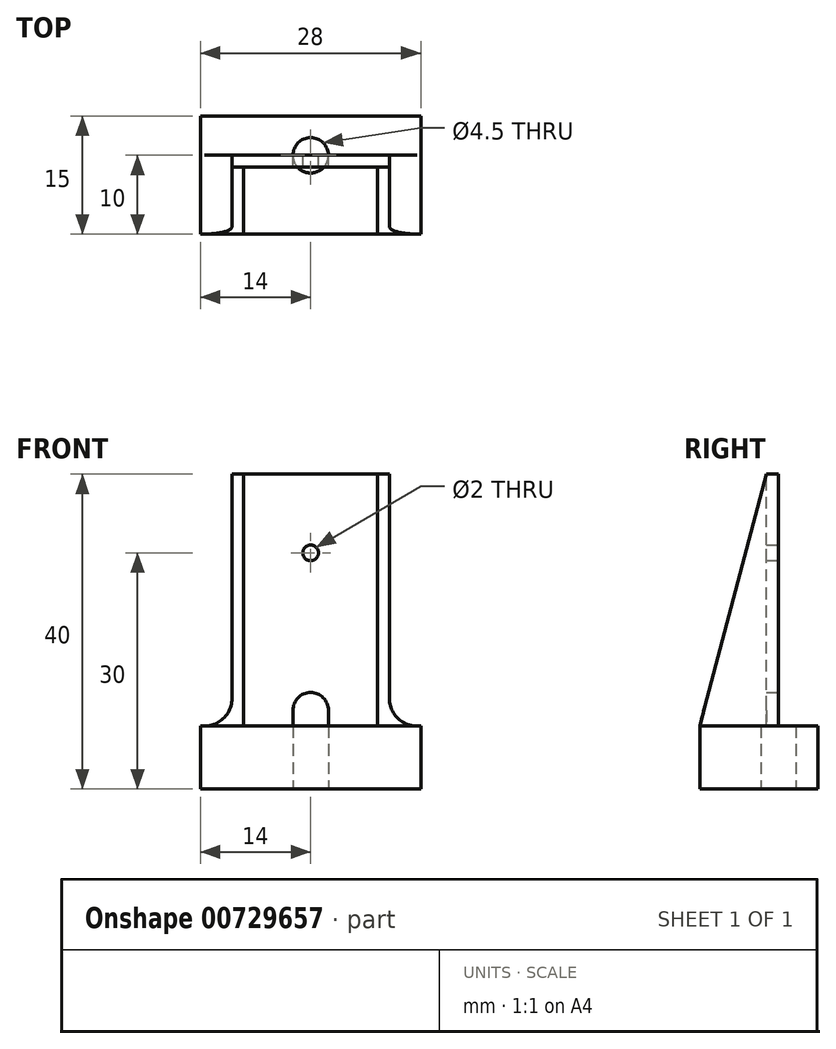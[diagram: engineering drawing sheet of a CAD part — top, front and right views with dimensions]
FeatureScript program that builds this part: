
annotation { "Feature Type Name" : "Feature", "Feature Type Description" : "" }
export const myFeature = defineFeature(function(context is Context, id is Id, definition is map)
    precondition{}
    {
        {
            var Q0;
            Q0=qCreatedBy(makeId("Front.planeOp"),FACE);
            var sketch = newSketch(context, id + "F0", { "sketchPlane" : qUnion([Q0])});
            skLineSegment(sketch, "E0.bottom", {"start": v(-14, 0) * mm, "end": v(14, 0) * mm});
            skLineSegment(sketch, "E0.top", {"start": v(-14, 40) * mm, "end": v(14, 40) * mm});
            skLineSegment(sketch, "E0.left", {"start": v(-14, 0) * mm, "end": v(-14, 40) * mm});
            skLineSegment(sketch, "E0.right", {"start": v(14, 0) * mm, "end": v(14, 40) * mm});
            skSolve(sketch);
        }
        {
            var Q0;
            Q0=makeQuery(id+"F0.imprint","IMPRINT",FACE,{"disambiguationData":[TD([[makeQuery(id+"F0.imprint","IMPRINT",EDGE,{"derivedFrom":sQuery(id+"F0.wireOp",EDGE,"E0.bottom")}),1.0]])]});
            extrude(context, id + "F1", {"entities" : qUnion([Q0]), "depth" : 10 * mm, "offsetDistance" : 25 * mm});
        }
        {
            var Q0;
            Q0=makeQuery(id+"F1.opExtrude","SWEPT_FACE",FACE,{"disambiguationData":[OSD([sQuery(id+"F0.wireOp",EDGE,"E0.top")])]});
            var sketch = newSketch(context, id + "F2", { "sketchPlane" : qUnion([Q0])});
            skLineSegment(sketch, "E1.bottom", {"start": v(-14, 0) * mm, "end": v(-10, 0) * mm});
            skLineSegment(sketch, "E1.top", {"start": v(-14, -10) * mm, "end": v(-10, -10) * mm});
            skLineSegment(sketch, "E1.left", {"start": v(-14, 0) * mm, "end": v(-14, -10) * mm});
            skLineSegment(sketch, "E1.right", {"start": v(-10, 0) * mm, "end": v(-10, -10) * mm});
            skLineSegment(sketch, "E2.bottom", {"start": v(14, 0) * mm, "end": v(10, 0) * mm});
            skLineSegment(sketch, "E2.top", {"start": v(14, -10) * mm, "end": v(10, -10) * mm});
            skLineSegment(sketch, "E2.left", {"start": v(14, 0) * mm, "end": v(14, -10) * mm});
            skLineSegment(sketch, "E2.right", {"start": v(10, 0) * mm, "end": v(10, -10) * mm});
            skLineSegment(sketch, "E3.bottom", {"start": v(-8.5, -10) * mm, "end": v(8.5, -10) * mm});
            skLineSegment(sketch, "E3.top", {"start": v(-8.5, -1.5) * mm, "end": v(8.5, -1.5) * mm});
            skLineSegment(sketch, "E3.left", {"start": v(-8.5, -10) * mm, "end": v(-8.5, -1.5) * mm});
            skLineSegment(sketch, "E3.right", {"start": v(8.5, -10) * mm, "end": v(8.5, -1.5) * mm});
            skSolve(sketch);
        }
        {
            var Q0;
            Q0 = qSketchRegion(id + "F2", true);
            extrude(context, id + "F3", {"entities" : qUnion([Q0]), "operationType" : NewBodyOperationType.REMOVE, "oppositeDirection" : true, "depth" : 32 * mm, "offsetDistance" : 25 * mm});
        }
        {
            var Q0;
            Q0=makeQuery(id+"F3.boolean.opBoolean","COPY",FACE,{"derivedFrom":makeQuery(id+"F3.opExtrude","SWEPT_FACE",FACE,{"disambiguationData":[OSD([sQuery(id+"F2.wireOp",EDGE,"E1.right")])]})});
            var sketch = newSketch(context, id + "F4", { "sketchPlane" : qUnion([Q0])});
            skLineSegment(sketch, "E4", {"start": v(10, 8) * mm, "end": v(1.5, 40) * mm});
            skLineSegment(sketch, "E5", {"start": v(1.5, 40) * mm, "end": v(10, 40) * mm});
            skLineSegment(sketch, "E6", {"start": v(10, 40) * mm, "end": v(10, 8) * mm});
            skSolve(sketch);
        }
        {
            var Q0;
            Q0 = qSketchRegion(id + "F4", true);
            extrude(context, id + "F5", {"entities" : qUnion([Q0]), "operationType" : NewBodyOperationType.REMOVE, "endBound" : BoundingType.THROUGH_ALL, "oppositeDirection" : true, "depth" : 25 * mm, "offsetDistance" : 25 * mm});
        }
        {
            var Q0;
            Q0=makeQuery(id+"F1.opExtrude","CAP_FACE",FACE,{"disambiguationData":[OSD([sQuery(id+"F0.wireOp",EDGE,"E0.bottom"),sQuery(id+"F0.wireOp",EDGE,"E0.top"),sQuery(id+"F0.wireOp",EDGE,"E0.left"),sQuery(id+"F0.wireOp",EDGE,"E0.right")])],"isStart":true});
            var sketch = newSketch(context, id + "F6", { "sketchPlane" : qUnion([Q0])});
            skLineSegment(sketch, "E7.bottom", {"start": v(-14, 0) * mm, "end": v(14, 0) * mm});
            skLineSegment(sketch, "E7.top", {"start": v(-14, 8) * mm, "end": v(14, 8) * mm});
            skLineSegment(sketch, "E7.left", {"start": v(-14, 0) * mm, "end": v(-14, 8) * mm});
            skLineSegment(sketch, "E7.right", {"start": v(14, 0) * mm, "end": v(14, 8) * mm});
            skSolve(sketch);
        }
        {
            var Q0;
            Q0 = qSketchRegion(id + "F6", true);
            extrude(context, id + "F7", {"entities" : qUnion([Q0]), "operationType" : NewBodyOperationType.ADD, "depth" : 5 * mm, "offsetDistance" : 25 * mm});
        }
        {
            var Q0;
            Q0=makeQuery(id+"F1.opExtrude","CAP_FACE",FACE,{"disambiguationData":[OSD([sQuery(id+"F0.wireOp",EDGE,"E0.bottom"),sQuery(id+"F0.wireOp",EDGE,"E0.top"),sQuery(id+"F0.wireOp",EDGE,"E0.left"),sQuery(id+"F0.wireOp",EDGE,"E0.right")])],"isStart":true});
            var sketch = newSketch(context, id + "F8", { "sketchPlane" : qUnion([Q0])});
            skCircle(sketch, "E8", {"center": v(0, 30) * mm, "radius": 1 * mm});
            skSolve(sketch);
        }
        {
            var Q0;
            Q0 = qSketchRegion(id + "F8", true);
            extrude(context, id + "F9", {"entities" : qUnion([Q0]), "operationType" : NewBodyOperationType.REMOVE, "endBound" : BoundingType.THROUGH_ALL, "oppositeDirection" : true, "depth" : 25 * mm, "offsetDistance" : 25 * mm});
        }
        {
            var Q0;
            Q0=makeQuery(id+"F7.boolean.opBoolean","MERGE",FACE,{"derivedFrom":[makeQuery(id+"F1.opExtrude","SWEPT_FACE",FACE,{"disambiguationData":[OSD([sQuery(id+"F0.wireOp",EDGE,"E0.bottom")])]}),makeQuery(id+"F7.opExtrude","SWEPT_FACE",FACE,{"disambiguationData":[OSD([sQuery(id+"F6.wireOp",EDGE,"E7.bottom")])]})]});
            var sketch = newSketch(context, id + "F10", { "sketchPlane" : qUnion([Q0])});
            skCircle(sketch, "E9", {"center": v(0, 0) * mm, "radius": 2.25 * mm});
            skSolve(sketch);
        }
        {
            var Q0;
            Q0 = qSketchRegion(id + "F10", true);
            extrude(context, id + "F11", {"entities" : qUnion([Q0]), "operationType" : NewBodyOperationType.REMOVE, "oppositeDirection" : true, "depth" : 9 * mm, "offsetDistance" : 25 * mm});
        }
        {
            var Q0;
            Q0=makeQuery(id+"F1.opExtrude","CAP_FACE",FACE,{"disambiguationData":[OSD([sQuery(id+"F0.wireOp",EDGE,"E0.bottom"),sQuery(id+"F0.wireOp",EDGE,"E0.top"),sQuery(id+"F0.wireOp",EDGE,"E0.left"),sQuery(id+"F0.wireOp",EDGE,"E0.right")])],"isStart":true});
            var sketch = newSketch(context, id + "F12", { "sketchPlane" : qUnion([Q0])});
            skLineSegment(sketch, "E10.bottom", {"start": v(-2.25, 8) * mm, "end": v(2.25, 8) * mm});
            skLineSegment(sketch, "E10.left", {"start": v(-2.25, 8) * mm, "end": v(-2.25, 10) * mm});
            skLineSegment(sketch, "E10.right", {"start": v(2.25, 8) * mm, "end": v(2.25, 10) * mm});
            skArc(sketch, "E11", {"start": v(-2.25, 10) * mm, "mid": v(0, 12.25) * mm, "end": v(2.25, 10) * mm});
            skSolve(sketch);
        }
        {
            var Q0;
            Q0 = qSketchRegion(id + "F12", true);
            extrude(context, id + "F13", {"entities" : qUnion([Q0]), "operationType" : NewBodyOperationType.REMOVE, "endBound" : BoundingType.THROUGH_ALL, "oppositeDirection" : true, "depth" : 25 * mm, "offsetDistance" : 25 * mm});
        }
        {
            var Q0;
            Q0=makeQuery(id+"F3.boolean.opBoolean","COPY",EDGE,{"derivedFrom":makeQuery(id+"F3.opExtrude","CAP_EDGE",EDGE,{"disambiguationData":[OSD([sQuery(id+"F2.wireOp",EDGE,"E2.right")])],"isStart":false})});
            var Q1;
            Q1=makeQuery(id+"F3.boolean.opBoolean","COPY",EDGE,{"derivedFrom":makeQuery(id+"F3.opExtrude","CAP_EDGE",EDGE,{"disambiguationData":[OSD([sQuery(id+"F2.wireOp",EDGE,"E1.right")])],"isStart":false})});
            fillet(context, id + "F14", {"entities" : qUnion([Q0, Q1]), "radius" : 3.5 * mm, "tangentPropagation" : true, "allowEdgeOverflow" : false});
        }
    });
